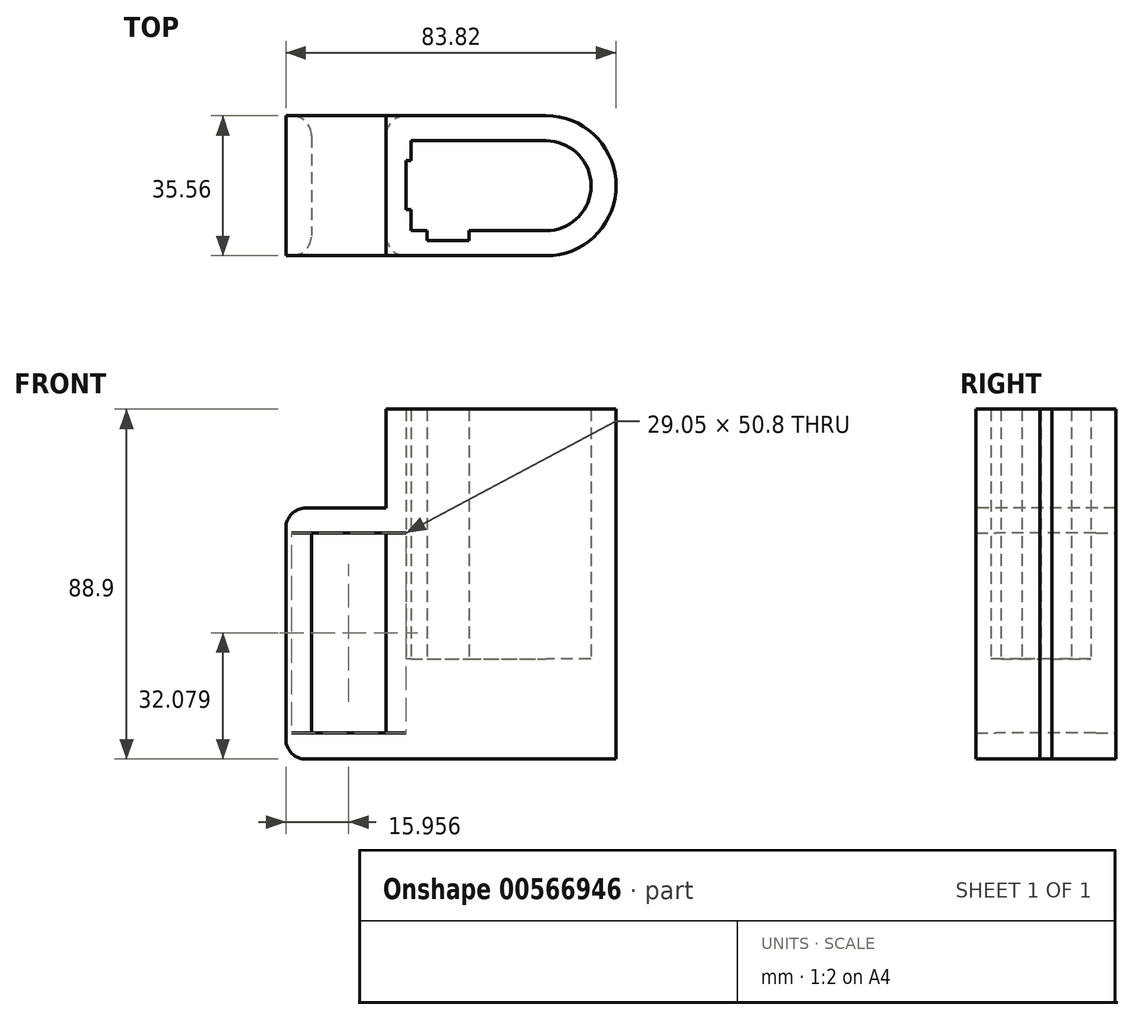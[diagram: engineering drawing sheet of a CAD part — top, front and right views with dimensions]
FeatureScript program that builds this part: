
annotation { "Feature Type Name" : "Feature", "Feature Type Description" : "" }
export const myFeature = defineFeature(function(context is Context, id is Id, definition is map)
    precondition{}
    {
        {
            var Q0;
            Q0=qCreatedBy(makeId("Top.planeOp"),FACE);
            var sketch = newSketch(context, id + "F0", { "sketchPlane" : qUnion([Q0])});
            skLineSegment(sketch, "E0.bottom", {"start": v(-64.07, 10.83) * mm, "end": v(-29.71, 10.83) * mm});
            skLineSegment(sketch, "E0.left", {"start": v(-64.07, 10.83) * mm, "end": v(-64.07, 5.85) * mm});
            skLineSegment(sketch, "E0.right", {"start": v(-18.35, 0.62) * mm, "end": v(-18.35, -1.82) * mm});
            skArc(sketch, "E1", {"start": v(-29.71, -12.03) * mm, "mid": v(-18.28, -0.6) * mm, "end": v(-29.71, 10.83) * mm});
            skLineSegment(sketch, "E2.bottom", {"start": v(-64.07, 5.85) * mm, "end": v(-65.24, 5.85) * mm});
            skLineSegment(sketch, "E2.top", {"start": v(-64.07, -6.7) * mm, "end": v(-65.24, -6.7) * mm});
            skLineSegment(sketch, "E2.right", {"start": v(-65.24, 5.85) * mm, "end": v(-65.24, -6.7) * mm});
            skLineSegment(sketch, "E3.trimOffspring", {"start": v(-64.07, -6.7) * mm, "end": v(-64.07, -12.03) * mm});
            skLineSegment(sketch, "E4.trimOffspring", {"start": v(-49.27, -12.03) * mm, "end": v(-29.71, -12.03) * mm});
            skLineSegment(sketch, "E5", {"start": v(-64.07, -12.03) * mm, "end": v(-60.02, -12.03) * mm});
            skLineSegment(sketch, "E6.top", {"start": v(-60.02, -14.51) * mm, "end": v(-49.27, -14.51) * mm});
            skLineSegment(sketch, "E6.left", {"start": v(-60.02, -12.03) * mm, "end": v(-60.02, -14.51) * mm});
            skLineSegment(sketch, "E6.right", {"start": v(-49.27, -12.03) * mm, "end": v(-49.27, -14.51) * mm});
            skSolve(sketch);
        }
        {
            var Q0;
            Q0=qCreatedBy(makeId("Top.planeOp"),FACE);
            var sketch = newSketch(context, id + "F1", { "sketchPlane" : qUnion([Q0])});
            skArc(sketch, "E7.0", {"start": v(-29.71, -18.38) * mm, "mid": v(-17.7, -13.7) * mm, "end": v(-12, -2.12) * mm});
            skLineSegment(sketch, "E7.1", {"start": v(-42.92, -18.38) * mm, "end": v(-29.71, -18.38) * mm});
            skLineSegment(sketch, "E7.4", {"start": v(-70.42, 17.18) * mm, "end": v(-70.42, 12.2) * mm});
            skLineSegment(sketch, "E7.5", {"start": v(-29.71, 17.18) * mm, "end": v(-70.42, 17.18) * mm});
            skArc(sketch, "E7.6", {"start": v(-12, 0.92) * mm, "mid": v(-17.7, 12.5) * mm, "end": v(-29.71, 17.18) * mm});
            skLineSegment(sketch, "E7.9", {"start": v(-70.42, -13.05) * mm, "end": v(-70.42, -18.38) * mm});
            skLineSegment(sketch, "E7.10", {"start": v(-12, -2.12) * mm, "end": v(-12, 0.92) * mm});
            skLineSegment(sketch, "E7.11", {"start": v(-70.42, -18.38) * mm, "end": v(-66.37, -18.38) * mm});
            skLineSegment(sketch, "E8", {"start": v(-70.42, 12.2) * mm, "end": v(-70.42, -13.05) * mm});
            skLineSegment(sketch, "E9", {"start": v(-66.37, -18.38) * mm, "end": v(-42.92, -18.38) * mm});
            skSolve(sketch);
        }
        {
            var Q0;
            {var subQ0=sQuery(id+"F0.wireOp",EDGE,"E0.right");Q0=makeQuery(id+"F0.imprint","IMPRINT",FACE,{"disambiguationData":[TD([[makeQuery(id+"F0.imprint","IMPRINT",EDGE,{"derivedFrom":subQ0}),1.0]])]});}
            var Q1;
            {var subQ2=sQuery(id+"F0.wireOp",EDGE,"E0.bottom");Q1=makeQuery(id+"F0.imprint","IMPRINT",FACE,{"disambiguationData":[TD([[makeQuery(id+"F0.imprint","IMPRINT",EDGE,{"derivedFrom":subQ2}),-1.0]])]});}
            extrude(context, id + "F2", {"entities" : qUnion([Q0, Q1]), "oppositeDirection" : true, "depth" : 6.35 * mm, "offsetDistance" : 25.4 * mm});
        }
        {
            var Q0;
            Q0=makeQuery(id+"F1.imprint","IMPRINT",FACE,{"disambiguationData":[TD([[makeQuery(id+"F1.imprint","IMPRINT",EDGE,{"derivedFrom":sQuery(id+"F1.wireOp",EDGE,"E7.0")}),1.0]])]});
            extrude(context, id + "F3", {"entities" : qUnion([Q0]), "operationType" : NewBodyOperationType.ADD, "oppositeDirection" : true, "depth" : 25.4 * mm, "offsetDistance" : 25.4 * mm});
        }
        {
            var Q0;
            {var subQ2=sQuery(id+"F0.wireOp",EDGE,"E0.bottom");Q0=makeQuery(id+"F0.imprint","IMPRINT",FACE,{"disambiguationData":[TD([[makeQuery(id+"F0.imprint","IMPRINT",EDGE,{"derivedFrom":subQ2}),-1.0]])]});}
            var sketch = newSketch(context, id + "F4", { "sketchPlane" : qUnion([Q0])});
            skArc(sketch, "E10.0", {"start": v(-29.71, -18.38) * mm, "mid": v(-17.7, -13.7) * mm, "end": v(-12, -2.12) * mm});
            skLineSegment(sketch, "E10.1", {"start": v(-42.92, -18.38) * mm, "end": v(-29.71, -18.38) * mm});
            skLineSegment(sketch, "E10.4", {"start": v(-70.42, 17.18) * mm, "end": v(-70.42, 12.2) * mm});
            skLineSegment(sketch, "E10.5", {"start": v(-29.71, 17.18) * mm, "end": v(-70.42, 17.18) * mm});
            skArc(sketch, "E10.6", {"start": v(-12, 0.92) * mm, "mid": v(-17.7, 12.5) * mm, "end": v(-29.71, 17.18) * mm});
            skLineSegment(sketch, "E10.9", {"start": v(-70.42, -13.05) * mm, "end": v(-70.42, -18.38) * mm});
            skLineSegment(sketch, "E10.10", {"start": v(-12, -2.12) * mm, "end": v(-12, 0.92) * mm});
            skLineSegment(sketch, "E10.11", {"start": v(-70.42, -18.38) * mm, "end": v(-66.37, -18.38) * mm});
            skLineSegment(sketch, "E11.0", {"start": v(-64.07, 5.85) * mm, "end": v(-65.24, 5.85) * mm});
            skLineSegment(sketch, "E11.1", {"start": v(-64.07, 10.83) * mm, "end": v(-64.07, 5.85) * mm});
            skLineSegment(sketch, "E11.2", {"start": v(-29.71, 10.83) * mm, "end": v(-64.07, 10.83) * mm});
            skLineSegment(sketch, "E11.3", {"start": v(-60.02, -12.03) * mm, "end": v(-60.02, -14.51) * mm});
            skLineSegment(sketch, "E11.4", {"start": v(-64.07, -12.03) * mm, "end": v(-60.02, -12.03) * mm});
            skLineSegment(sketch, "E11.5", {"start": v(-64.07, -6.7) * mm, "end": v(-64.07, -12.03) * mm});
            skLineSegment(sketch, "E11.6", {"start": v(-65.24, -6.7) * mm, "end": v(-64.07, -6.7) * mm});
            skLineSegment(sketch, "E11.7", {"start": v(-60.02, -14.51) * mm, "end": v(-49.27, -14.51) * mm});
            skLineSegment(sketch, "E11.8", {"start": v(-49.27, -14.51) * mm, "end": v(-49.27, -12.03) * mm});
            skLineSegment(sketch, "E11.9", {"start": v(-49.27, -12.03) * mm, "end": v(-29.71, -12.03) * mm});
            skLineSegment(sketch, "E11.10", {"start": v(-65.24, 5.85) * mm, "end": v(-65.24, -6.7) * mm});
            skArc(sketch, "E11.11", {"start": v(-29.71, -12.03) * mm, "mid": v(-22.07, -9.1) * mm, "end": v(-18.35, -1.82) * mm});
            skLineSegment(sketch, "E11.12", {"start": v(-18.35, -1.82) * mm, "end": v(-18.35, 0.62) * mm});
            skArc(sketch, "E11.13", {"start": v(-18.35, 0.62) * mm, "mid": v(-22.07, 7.9) * mm, "end": v(-29.71, 10.83) * mm});
            skLineSegment(sketch, "E12", {"start": v(-70.42, 12.2) * mm, "end": v(-70.42, -13.05) * mm});
            skLineSegment(sketch, "E13", {"start": v(-66.37, -18.38) * mm, "end": v(-42.92, -18.38) * mm});
            skSolve(sketch);
        }
        {
            var Q0;
            Q0 = qSketchRegion(id + "F4", true);
            extrude(context, id + "F5", {"entities" : qUnion([Q0]), "operationType" : NewBodyOperationType.ADD, "depth" : 63.5 * mm, "offsetDistance" : 25.4 * mm});
        }
        {
            var Q0;
            Q0=makeQuery(id+"F5.boolean.opBoolean","MERGE",FACE,{"derivedFrom":[makeQuery(id+"F3.opExtrude","SWEPT_FACE",FACE,{"disambiguationData":[OSD([sQuery(id+"F1.wireOp",EDGE,"E7.4"),sQuery(id+"F1.wireOp",EDGE,"E7.9"),sQuery(id+"F1.wireOp",EDGE,"E8")])]}),makeQuery(id+"F5.opExtrude","SWEPT_FACE",FACE,{"disambiguationData":[OSD([sQuery(id+"F4.wireOp",EDGE,"E10.4"),sQuery(id+"F4.wireOp",EDGE,"E10.9"),sQuery(id+"F4.wireOp",EDGE,"E12")])]})]});
            var sketch = newSketch(context, id + "F6", { "sketchPlane" : qUnion([Q0])});
            skLineSegment(sketch, "E14", {"start": v(0.6, 63.5) * mm, "end": v(0.6, 44.45) * mm});
            skLineSegment(sketch, "E15.bottom", {"start": v(-17.18, -18.72) * mm, "end": v(18.38, -18.72) * mm});
            skLineSegment(sketch, "E15.top", {"start": v(-17.18, -25.4) * mm, "end": v(18.38, -25.4) * mm});
            skLineSegment(sketch, "E15.left", {"start": v(-17.18, -18.72) * mm, "end": v(-17.18, -25.4) * mm});
            skLineSegment(sketch, "E15.right", {"start": v(18.38, -18.72) * mm, "end": v(18.38, -25.4) * mm});
            skSolve(sketch);
        }
        {
            var Q0;
            Q0=makeQuery(id+"F6.imprint","IMPRINT",FACE,{"disambiguationData":[TD([[makeQuery(id+"F6.imprint","IMPRINT",EDGE,{"derivedFrom":sQuery(id+"F6.wireOp",EDGE,"E15.bottom")}),-1.0]])]});
            extrude(context, id + "F7", {"entities" : qUnion([Q0]), "operationType" : NewBodyOperationType.ADD, "depth" : 25.4 * mm, "offsetDistance" : 25.4 * mm});
        }
        {
            var Q0;
            Q0=makeQuery(id+"F7.opExtrude","SWEPT_FACE",FACE,{"disambiguationData":[OSD([sQuery(id+"F6.wireOp",EDGE,"E15.bottom")])]});
            var sketch = newSketch(context, id + "F8", { "sketchPlane" : qUnion([Q0])});
            skLineSegment(sketch, "E16.bottom", {"start": v(-95.82, 17.18) * mm, "end": v(-89.3, 17.18) * mm});
            skLineSegment(sketch, "E16.top", {"start": v(-95.82, -18.38) * mm, "end": v(-89.3, -18.38) * mm});
            skLineSegment(sketch, "E16.left", {"start": v(-95.82, 17.18) * mm, "end": v(-95.82, -18.38) * mm});
            skLineSegment(sketch, "E16.right", {"start": v(-89.3, 17.18) * mm, "end": v(-89.3, -18.38) * mm});
            skSolve(sketch);
        }
        {
            var Q0;
            Q0=makeQuery(id+"F8.imprint","IMPRINT",FACE,{"disambiguationData":[TD([[makeQuery(id+"F8.imprint","IMPRINT",EDGE,{"derivedFrom":sQuery(id+"F8.wireOp",EDGE,"E16.bottom")}),-1.0]])]});
            extrude(context, id + "F9", {"entities" : qUnion([Q0]), "operationType" : NewBodyOperationType.ADD, "depth" : 57.15 * mm, "offsetDistance" : 25.4 * mm});
        }
        {
            var Q0;
            Q0=makeQuery(id+"F9.opExtrude","SWEPT_FACE",FACE,{"disambiguationData":[OSD([sQuery(id+"F8.wireOp",EDGE,"E16.right")])]});
            var sketch = newSketch(context, id + "F10", { "sketchPlane" : qUnion([Q0])});
            skLineSegment(sketch, "E17.bottom", {"start": v(17.18, 38.43) * mm, "end": v(-18.38, 38.43) * mm});
            skLineSegment(sketch, "E17.top", {"start": v(17.18, 32.08) * mm, "end": v(-18.38, 32.08) * mm});
            skLineSegment(sketch, "E17.left", {"start": v(17.18, 38.43) * mm, "end": v(17.18, 32.08) * mm});
            skLineSegment(sketch, "E17.right", {"start": v(-18.38, 38.43) * mm, "end": v(-18.38, 32.08) * mm});
            skSolve(sketch);
        }
        {
            var Q0;
            Q0=makeQuery(id+"F10.imprint","IMPRINT",FACE,{"disambiguationData":[TD([[makeQuery(id+"F10.imprint","IMPRINT",EDGE,{"derivedFrom":sQuery(id+"F10.wireOp",EDGE,"E17.bottom")}),1.0]])]});
            extrude(context, id + "F11", {"entities" : qUnion([Q0]), "operationType" : NewBodyOperationType.ADD, "depth" : 19.05 * mm, "offsetDistance" : 25.4 * mm});
        }
        {
            var Q0;
            Q0=makeQuery(id+"F9.opExtrude","CAP_EDGE",EDGE,{"disambiguationData":[OSD([sQuery(id+"F8.wireOp",EDGE,"E16.left")])],"isStart":false});
            fillet(context, id + "F12", {"entities" : qUnion([Q0]), "radius" : 5.08 * mm, "tangentPropagation" : true, "allowEdgeOverflow" : false});
        }
        {
            var Q0;
            Q0=makeQuery(id+"F7.opExtrude","CAP_EDGE",EDGE,{"disambiguationData":[OSD([sQuery(id+"F6.wireOp",EDGE,"E15.top")])],"isStart":false});
            fillet(context, id + "F13", {"entities" : qUnion([Q0]), "radius" : 5.08 * mm, "tangentPropagation" : true, "allowEdgeOverflow" : false});
        }
        {
            var Q0;
            Q0=makeQuery(id+"F9.opExtrude","SWEPT_EDGE",EDGE,{"disambiguationData":[OSD([sQuery(id+"F1.wireOp",EDGE,"E7.9"),sQuery(id+"F1.wireOp",EDGE,"E7.11"),sQuery(id+"F4.wireOp",EDGE,"E10.9"),sQuery(id+"F4.wireOp",EDGE,"E10.11"),sQuery(id+"F6.wireOp",EDGE,"E15.bottom"),sQuery(id+"F6.wireOp",EDGE,"E15.right"),sQuery(id+"F8.wireOp",EDGE,"E16.top"),sQuery(id+"F8.wireOp",EDGE,"E16.right")])]});
            fillet(context, id + "F14", {"entities" : qUnion([Q0]), "radius" : 5.08 * mm, "tangentPropagation" : true, "allowEdgeOverflow" : false});
        }
        {
            var Q0;
            Q0=makeQuery(id+"F9.opExtrude","SWEPT_EDGE",EDGE,{"disambiguationData":[OSD([sQuery(id+"F1.wireOp",EDGE,"E7.4"),sQuery(id+"F1.wireOp",EDGE,"E7.5"),sQuery(id+"F4.wireOp",EDGE,"E10.4"),sQuery(id+"F4.wireOp",EDGE,"E10.5"),sQuery(id+"F6.wireOp",EDGE,"E15.bottom"),sQuery(id+"F6.wireOp",EDGE,"E15.left"),sQuery(id+"F8.wireOp",EDGE,"E16.bottom"),sQuery(id+"F8.wireOp",EDGE,"E16.right")])]});
            fillet(context, id + "F15", {"entities" : qUnion([Q0]), "radius" : 5.08 * mm, "tangentPropagation" : true, "allowEdgeOverflow" : false});
        }
        {
            var Q0;
            {var subQ0=sQuery(id+"F4.wireOp",EDGE,"E10.4");var subQ1=sQuery(id+"F1.wireOp",EDGE,"E7.5");var subQ2=sQuery(id+"F4.wireOp",EDGE,"E10.5");var subQ3=sQuery(id+"F1.wireOp",EDGE,"E7.4");Q0=makeQuery(id+"F11.boolean.opBoolean","SPLIT",EDGE,{"disambiguationData":[TD([makeQuery(id+"F7.opExtrude","SWEPT_FACE",FACE,{"disambiguationData":[OSD([sQuery(id+"F6.wireOp",EDGE,"E15.bottom")])]})])],"derivedFrom":makeQuery(id+"F5.boolean.opBoolean","MERGE",EDGE,{"derivedFrom":[makeQuery(id+"F3.opExtrude","SWEPT_EDGE",EDGE,{"disambiguationData":[OSD([subQ3,subQ1])]}),makeQuery(id+"F5.opExtrude","SWEPT_EDGE",EDGE,{"disambiguationData":[OSD([subQ0,subQ2])]})]})});}
            fillet(context, id + "F16", {"entities" : qUnion([Q0]), "radius" : 5.08 * mm, "tangentPropagation" : true, "allowEdgeOverflow" : false});
        }
        {
            var Q0;
            {var subQ0=sQuery(id+"F4.wireOp",EDGE,"E10.11");var subQ1=sQuery(id+"F1.wireOp",EDGE,"E7.9");var subQ2=sQuery(id+"F4.wireOp",EDGE,"E10.9");var subQ3=sQuery(id+"F1.wireOp",EDGE,"E7.11");Q0=makeQuery(id+"F11.boolean.opBoolean","SPLIT",EDGE,{"disambiguationData":[TD([makeQuery(id+"F7.opExtrude","SWEPT_FACE",FACE,{"disambiguationData":[OSD([sQuery(id+"F6.wireOp",EDGE,"E15.bottom")])]})])],"derivedFrom":makeQuery(id+"F5.boolean.opBoolean","MERGE",EDGE,{"derivedFrom":[makeQuery(id+"F3.opExtrude","SWEPT_EDGE",EDGE,{"disambiguationData":[OSD([subQ1,subQ3])]}),makeQuery(id+"F5.opExtrude","SWEPT_EDGE",EDGE,{"disambiguationData":[OSD([subQ2,subQ0])]})]})});}
            fillet(context, id + "F17", {"entities" : qUnion([Q0]), "radius" : 5.08 * mm, "tangentPropagation" : true, "allowEdgeOverflow" : false});
        }
    });
